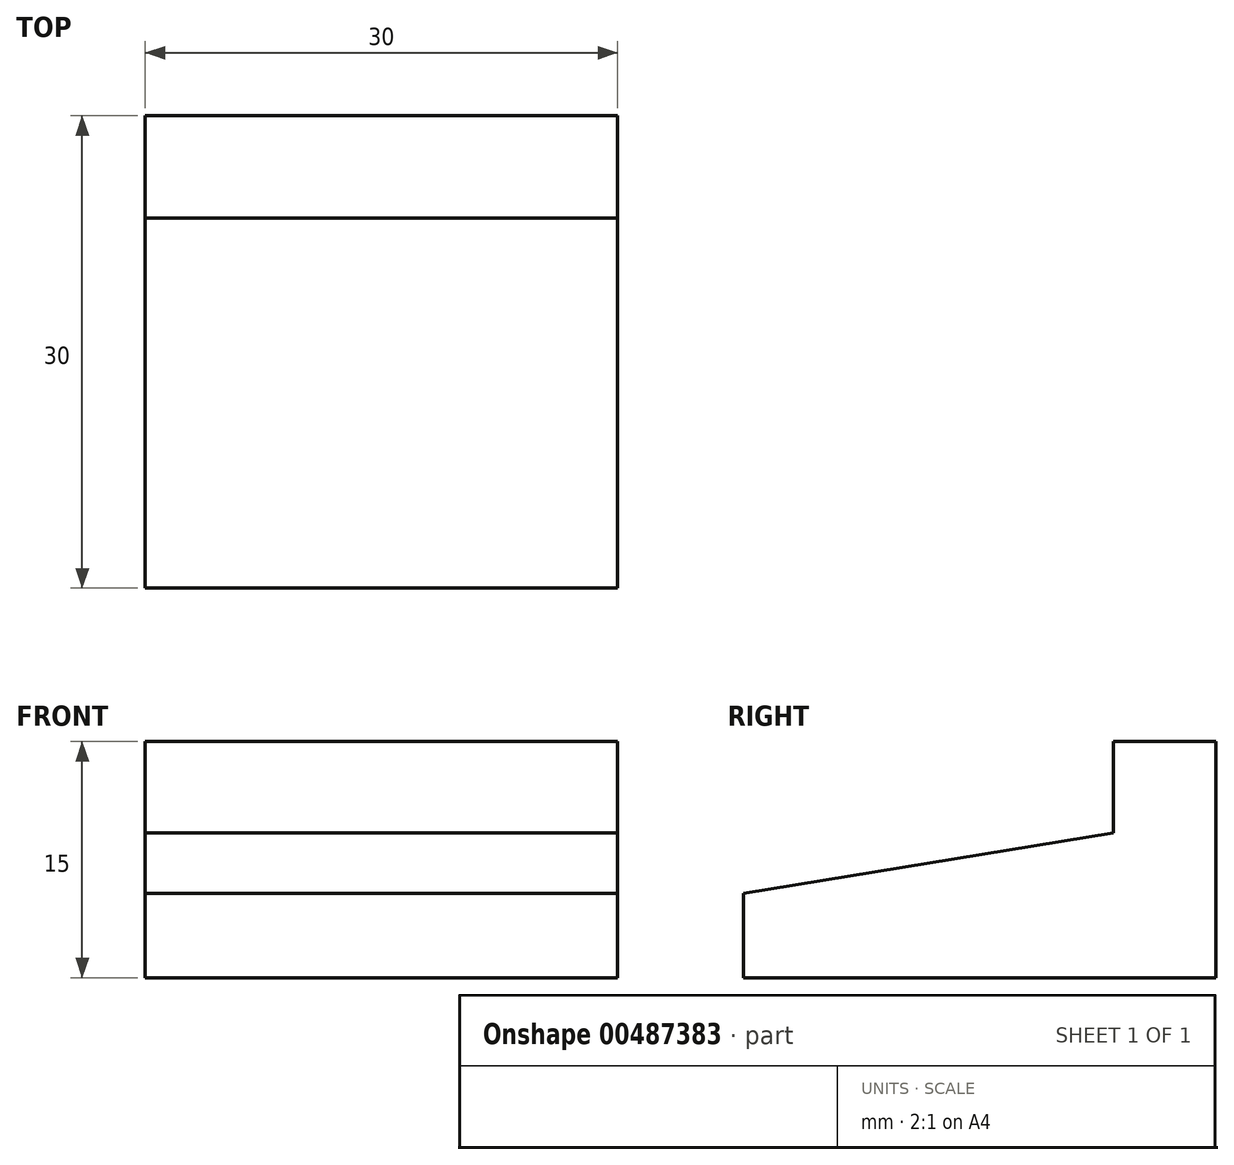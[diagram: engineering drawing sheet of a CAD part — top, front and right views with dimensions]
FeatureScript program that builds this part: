
annotation { "Feature Type Name" : "Feature", "Feature Type Description" : "" }
export const myFeature = defineFeature(function(context is Context, id is Id, definition is map)
    precondition{}
    {
        {
            var Q0;
            Q0=qCreatedBy(makeId("Top.planeOp"),FACE);
            var sketch = newSketch(context, id + "F0", { "sketchPlane" : qUnion([Q0])});
            skLineSegment(sketch, "E0.bottom", {"start": v(7.2, 27.43) * mm, "end": v(37.2, 27.43) * mm});
            skLineSegment(sketch, "E0.top", {"start": v(7.2, -2.57) * mm, "end": v(37.2, -2.57) * mm});
            skLineSegment(sketch, "E0.left", {"start": v(7.2, 27.43) * mm, "end": v(7.2, -2.57) * mm});
            skLineSegment(sketch, "E0.right", {"start": v(37.2, 27.43) * mm, "end": v(37.2, -2.57) * mm});
            skSolve(sketch);
        }
        {
            var Q0;
            Q0=makeQuery(id+"F0.imprint","IMPRINT",FACE,{"disambiguationData":[TD([[makeQuery(id+"F0.imprint","IMPRINT",EDGE,{"derivedFrom":sQuery(id+"F0.wireOp",EDGE,"E0.bottom")}),-1.0]])]});
            extrude(context, id + "F1", {"entities" : qUnion([Q0]), "depth" : 15 * mm});
        }
        {
            var Q0;
            Q0=makeQuery(id+"F1.opExtrude","SWEPT_FACE",FACE,{"disambiguationData":[OSD([sQuery(id+"F0.wireOp",EDGE,"E0.left")])]});
            var sketch = newSketch(context, id + "F2", { "sketchPlane" : qUnion([Q0])});
            skLineSegment(sketch, "E1", {"start": v(-27.43, 15) * mm, "end": v(-20.92, 15) * mm});
            skLineSegment(sketch, "E2", {"start": v(-20.92, 15) * mm, "end": v(-20.92, 9.21) * mm});
            skLineSegment(sketch, "E3", {"start": v(-20.92, 9.21) * mm, "end": v(2.57, 5.37) * mm});
            skLineSegment(sketch, "E4", {"start": v(2.57, 5.37) * mm, "end": v(2.57, 0) * mm});
            skSolve(sketch);
        }
        {
            var Q0;
            {var subQ0=sQuery(id+"F2.wireOp",EDGE,"E2");Q0=makeQuery(id+"F2.imprint","IMPRINT",FACE,{"disambiguationData":[TD([[makeQuery(id+"F2.imprint","IMPRINT",EDGE,{"derivedFrom":subQ0}),1.0]])]});}
            extrude(context, id + "F3", {"entities" : qUnion([Q0]), "operationType" : NewBodyOperationType.REMOVE, "endBound" : BoundingType.THROUGH_ALL, "oppositeDirection" : true, "depth" : 25 * mm});
        }
    });
